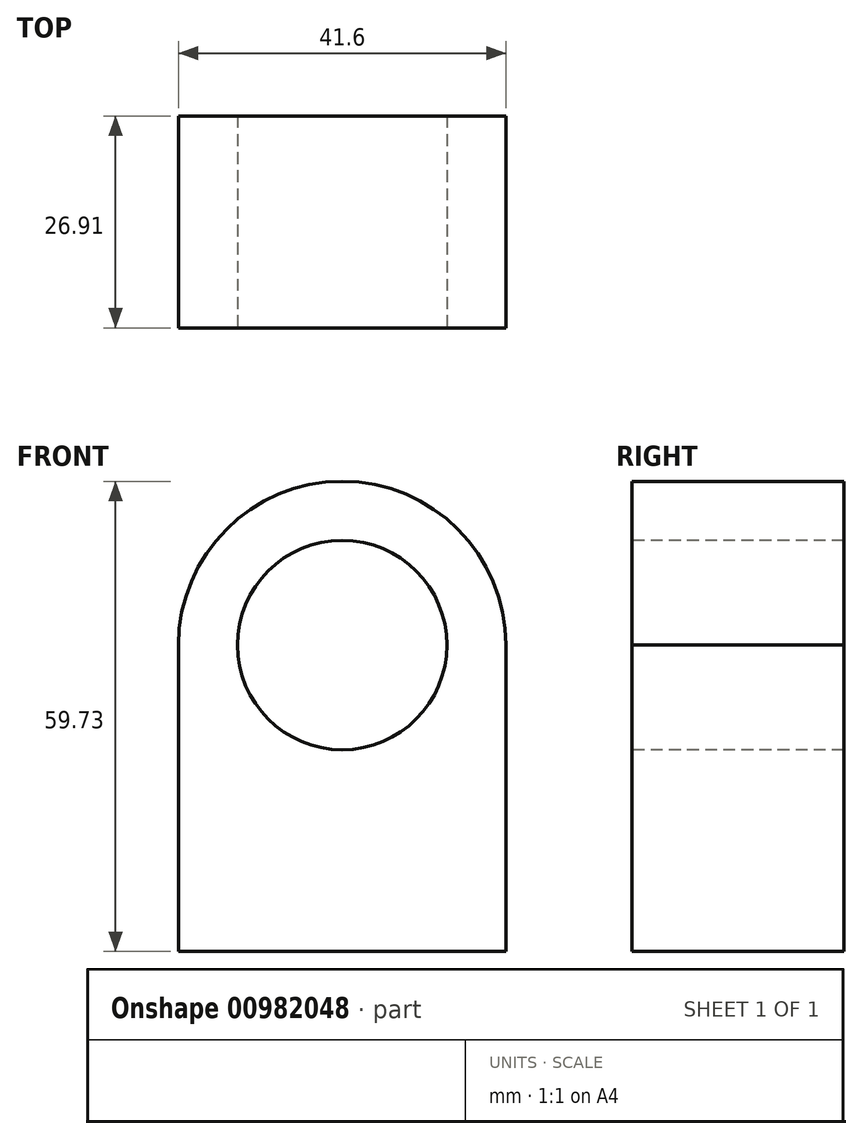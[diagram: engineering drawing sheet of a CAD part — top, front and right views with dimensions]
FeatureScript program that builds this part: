
annotation { "Feature Type Name" : "Feature", "Feature Type Description" : "" }
export const myFeature = defineFeature(function(context is Context, id is Id, definition is map)
    precondition{}
    {
        {
            var Q0;
            Q0=qCreatedBy(makeId("Front.planeOp"),FACE);
            var sketch = newSketch(context, id + "F0", { "sketchPlane" : qUnion([Q0])});
            skCircle(sketch, "E0", {"center": v(0, 0) * mm, "radius": 13.3 * mm});
            skArc(sketch, "E1", {"start": v(20.8, 0) * mm, "mid": v(0, 20.8) * mm, "end": v(-20.8, 0) * mm});
            skLineSegment(sketch, "E2.top", {"start": v(-20.8, -38.93) * mm, "end": v(20.79, -38.93) * mm});
            skLineSegment(sketch, "E2.left", {"start": v(-20.8, 0) * mm, "end": v(-20.8, -38.93) * mm});
            skLineSegment(sketch, "E2.right", {"start": v(20.79, 0) * mm, "end": v(20.79, -38.93) * mm});
            skSolve(sketch);
        }
        {
            var Q0;
            Q0=sQuery(id+"F0.wireOp",EDGE,"E2.right");
            var Q1;
            Q1=sQuery(id+"F0.wireOp",EDGE,"E1");
            var Q2;
            Q2=sQuery(id+"F0.wireOp",EDGE,"E2.left");
            var Q3;
            Q3=sQuery(id+"F0.wireOp",EDGE,"E2.top");
            var Q4;
            Q4=sQuery(id+"F0.wireOp",EDGE,"E0");
            extrude(context, id + "F1", {"bodyType" : ToolBodyType.SURFACE, "surfaceEntities" : qUnion([Q0, Q1, Q2, Q3, Q4]), "depth" : 26.91 * mm, "offsetDistance" : 25.4 * mm});
        }
    });
